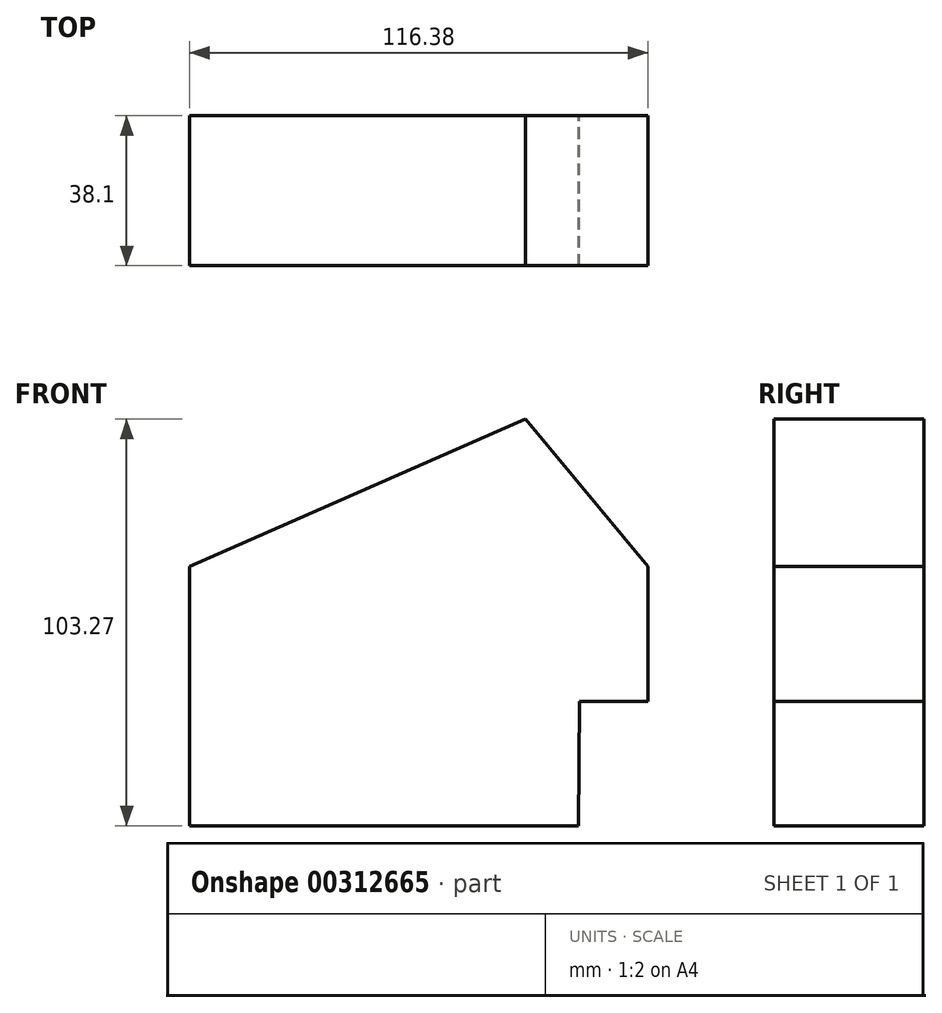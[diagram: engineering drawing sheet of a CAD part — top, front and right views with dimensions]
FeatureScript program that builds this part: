
annotation { "Feature Type Name" : "Feature", "Feature Type Description" : "" }
export const myFeature = defineFeature(function(context is Context, id is Id, definition is map)
    precondition{}
    {
        {
            var Q0;
            Q0=qCreatedBy(makeId("Front.planeOp"),FACE);
            var sketch = newSketch(context, id + "F0", { "sketchPlane" : qUnion([Q0])});
            skLineSegment(sketch, "E0", {"start": v(-53.24, -43.8) * mm, "end": v(-53.24, 22.13) * mm});
            skLineSegment(sketch, "E1", {"start": v(-53.24, 22.13) * mm, "end": v(-38.07, 22.13) * mm});
            skLineSegment(sketch, "E2", {"start": v(-53.24, -43.8) * mm, "end": v(45.5, -43.8) * mm});
            skLineSegment(sketch, "E3", {"start": v(45.5, -43.8) * mm, "end": v(45.8, -7.58) * mm});
            skLineSegment(sketch, "E4", {"start": v(45.8, -7.58) * mm, "end": v(61.28, 7.27) * mm});
            skLineSegment(sketch, "E5", {"start": v(61.28, 7.27) * mm, "end": v(15.48, -7.58) * mm});
            skLineSegment(sketch, "E6", {"start": v(15.48, -7.58) * mm, "end": v(15.48, -29.25) * mm});
            skLineSegment(sketch, "E7", {"start": v(15.48, -29.25) * mm, "end": v(-37.76, -29.25) * mm});
            skLineSegment(sketch, "E8", {"start": v(-37.76, -29.25) * mm, "end": v(-37.76, 22.13) * mm});
            skLineSegment(sketch, "E9", {"start": v(-37.76, 22.13) * mm, "end": v(63.14, 22.13) * mm});
            skLineSegment(sketch, "E10", {"start": v(63.14, 22.13) * mm, "end": v(32.03, 59.47) * mm});
            skLineSegment(sketch, "E11", {"start": v(32.03, 59.47) * mm, "end": v(-53.24, 22.13) * mm});
            skLineSegment(sketch, "E12", {"start": v(63.14, 22.13) * mm, "end": v(63.14, -12.23) * mm});
            skLineSegment(sketch, "E13", {"start": v(63.14, -12.23) * mm, "end": v(45.77, -12.23) * mm});
            skSolve(sketch);
        }
        {
            var Q0;
            Q0 = qSketchRegion(id + "F0", true);
            extrude(context, id + "F1", {"entities" : qUnion([Q0]), "depth" : 38.1 * mm});
        }
    });
